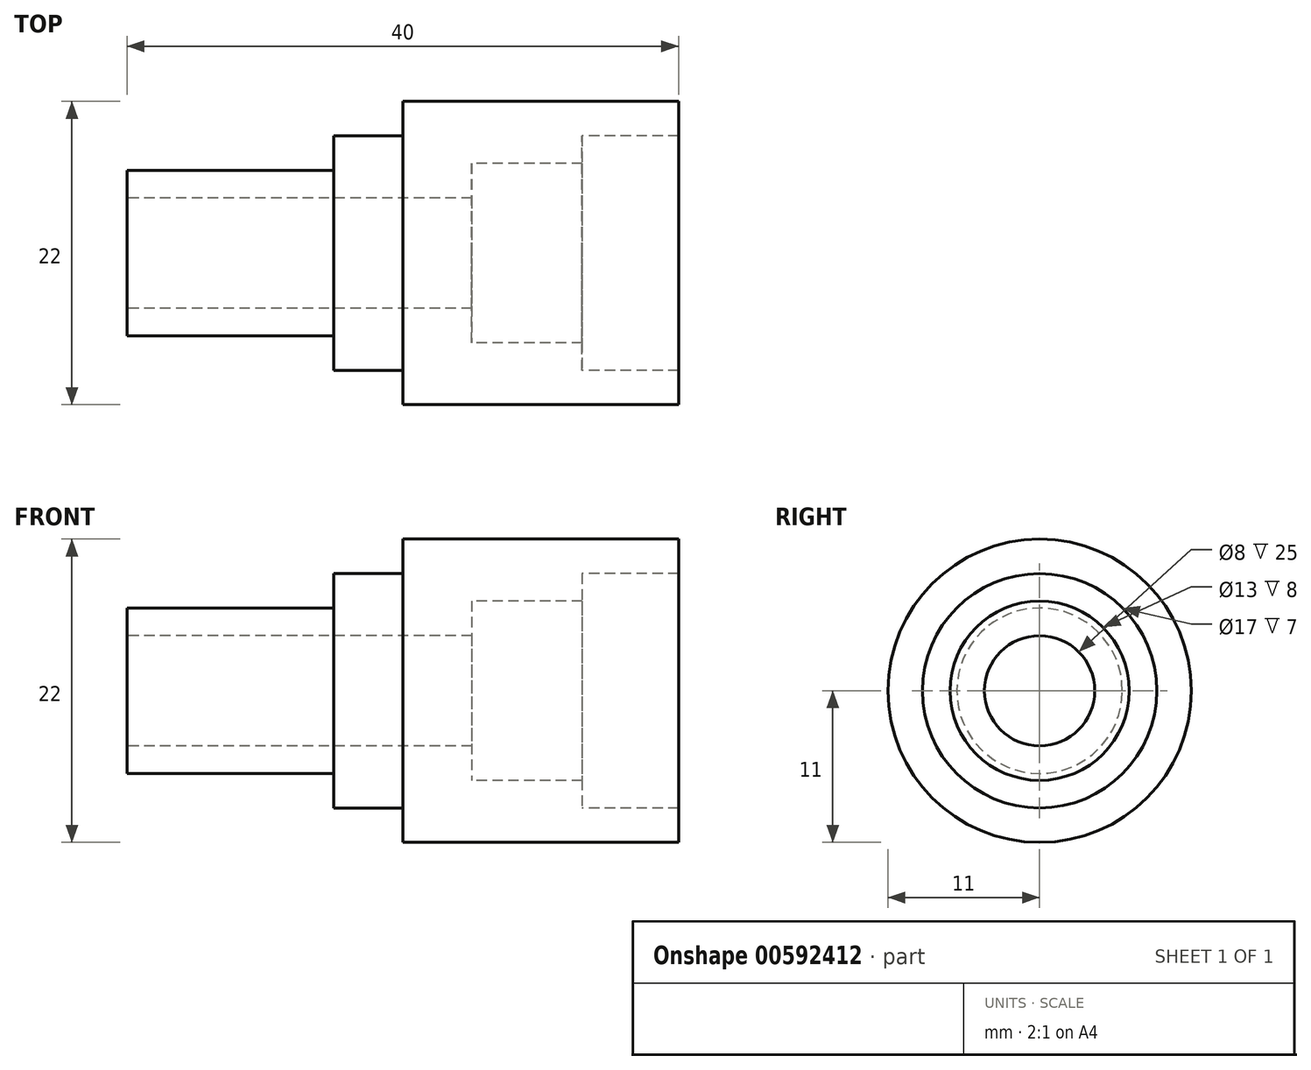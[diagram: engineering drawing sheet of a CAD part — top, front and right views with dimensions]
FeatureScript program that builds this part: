
annotation { "Feature Type Name" : "Feature", "Feature Type Description" : "" }
export const myFeature = defineFeature(function(context is Context, id is Id, definition is map)
    precondition{}
    {
        {
            var Q0;
            Q0=qCreatedBy(makeId("Front.planeOp"),FACE);
            var sketch = newSketch(context, id + "F0", { "sketchPlane" : qUnion([Q0])});
            skLineSegment(sketch, "E0", {"start": v(-18.07, 0) * mm, "end": v(21.93, 0) * mm, "construction": true});
            skLineSegment(sketch, "E1", {"start": v(-18.07, 4) * mm, "end": v(6.93, 4) * mm});
            skLineSegment(sketch, "E2", {"start": v(6.93, 4) * mm, "end": v(6.93, 6.5) * mm});
            skLineSegment(sketch, "E3", {"start": v(6.93, 6.5) * mm, "end": v(14.93, 6.5) * mm});
            skLineSegment(sketch, "E4", {"start": v(14.93, 6.5) * mm, "end": v(14.93, 8.5) * mm});
            skLineSegment(sketch, "E5", {"start": v(14.93, 8.5) * mm, "end": v(21.93, 8.5) * mm});
            skLineSegment(sketch, "E6", {"start": v(21.93, 8.5) * mm, "end": v(21.93, 11) * mm});
            skLineSegment(sketch, "E7", {"start": v(21.93, 11) * mm, "end": v(1.93, 11) * mm});
            skLineSegment(sketch, "E8", {"start": v(1.93, 11) * mm, "end": v(1.93, 8.5) * mm});
            skLineSegment(sketch, "E9", {"start": v(1.93, 8.5) * mm, "end": v(-3.07, 8.5) * mm});
            skLineSegment(sketch, "E10", {"start": v(-3.07, 8.5) * mm, "end": v(-3.07, 6) * mm});
            skLineSegment(sketch, "E11", {"start": v(-3.07, 6) * mm, "end": v(-18.07, 6) * mm});
            skLineSegment(sketch, "E12", {"start": v(-18.07, 6) * mm, "end": v(-18.07, 4) * mm});
            skSolve(sketch);
        }
        {
            var Q0;
            Q0 = qSketchRegion(id + "F0", true);
            var Q1;
            Q1=sQuery(id+"F0.wireOp",EDGE,"E0");
            revolve(context, id + "F1", {"entities" : qUnion([Q0]), "axis" : qUnion([Q1]), "revolveType" : RevolveType.FULL});
        }
    });
